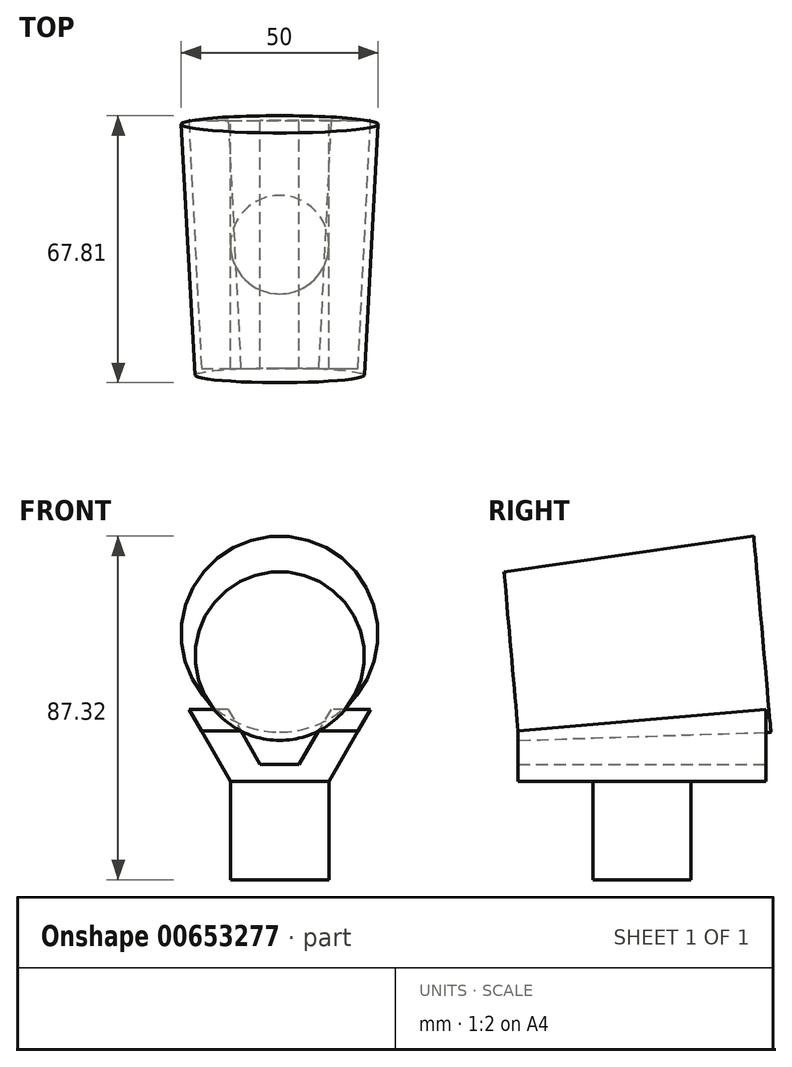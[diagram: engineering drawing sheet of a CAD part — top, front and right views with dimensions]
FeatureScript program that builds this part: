
annotation { "Feature Type Name" : "Feature", "Feature Type Description" : "" }
export const myFeature = defineFeature(function(context is Context, id is Id, definition is map)
    precondition{}
    {
        {
            var Q0;
            Q0=qCreatedBy(makeId("Top.planeOp"),FACE);
            var sketch = newSketch(context, id + "F0", { "sketchPlane" : qUnion([Q0])});
            skCircle(sketch, "E0", {"center": v(0, 0) * mm, "radius": 12.5 * mm});
            skPoint(sketch, "E1", {"position": v(12.5, 0) * mm});
            skPoint(sketch, "E2", {"position": v(-12.5, 0) * mm});
            skSolve(sketch);
        }
        {
            var Q0;
            Q0=qCreatedBy(makeId("Front.planeOp"),FACE);
            var sketch = newSketch(context, id + "F1", { "sketchPlane" : qUnion([Q0])});
            skLineSegment(sketch, "E3", {"start": v(12.5, 0) * mm, "end": v(23.08, 18.32) * mm});
            skLineSegment(sketch, "E4", {"start": v(23.08, 18.32) * mm, "end": v(13.05, 18.32) * mm});
            skLineSegment(sketch, "E5", {"start": v(-23.08, 18.32) * mm, "end": v(-12.5, 0) * mm});
            skLineSegment(sketch, "E6", {"start": v(0, -26.28) * mm, "end": v(0, 54.16) * mm, "construction": true});
            skLineSegment(sketch, "E7", {"start": v(13.05, 18.32) * mm, "end": v(4.94, 4.27) * mm});
            skLineSegment(sketch, "E8.MirrorCS", {"start": v(-13.05, 18.32) * mm, "end": v(-4.94, 4.27) * mm});
            skLineSegment(sketch, "E9.trimOffspring", {"start": v(-13.05, 18.32) * mm, "end": v(-23.08, 18.32) * mm});
            skLineSegment(sketch, "E10", {"start": v(4.94, 4.27) * mm, "end": v(-4.94, 4.27) * mm});
            skPoint(sketch, "E11.orphan", {"position": v(2.47, 0) * mm});
            skPoint(sketch, "E12.orphan", {"position": v(-2.47, 0) * mm});
            skLineSegment(sketch, "E13", {"start": v(-12.5, 0) * mm, "end": v(12.5, 0) * mm});
            skSolve(sketch);
        }
        {
            var Q0;
            Q0=makeQuery(id+"F0.imprint","IMPRINT",FACE,{"disambiguationData":[TD([[makeQuery(id+"F0.imprint","IMPRINT",EDGE,{"derivedFrom":sQuery(id+"F0.wireOp",EDGE,"E0")}),1.0]])]});
            extrude(context, id + "F2", {"entities" : qUnion([Q0]), "oppositeDirection" : true, "depth" : 25 * mm, "offsetDistance" : 25 * mm});
        }
        {
            var Q0;
            Q0=makeQuery(id+"F1.imprint","IMPRINT",FACE,{"disambiguationData":[TD([[makeQuery(id+"F1.imprint","IMPRINT",EDGE,{"derivedFrom":sQuery(id+"F1.wireOp",EDGE,"E3")}),1.0]])]});
            extrude(context, id + "F3", {"entities" : qUnion([Q0]), "operationType" : NewBodyOperationType.ADD, "endBound" : BoundingType.SYMMETRIC, "depth" : 63 * mm, "offsetDistance" : 25 * mm});
        }
        {
            var Q0;
            Q0=qCreatedBy(makeId("Right.planeOp"),FACE);
            var sketch = newSketch(context, id + "F4", { "sketchPlane" : qUnion([Q0])});
            skPoint(sketch, "E14.0", {"position": v(31.5, 18.32) * mm});
            skLineSegment(sketch, "E15.0", {"start": v(-31.5, 18.32) * mm, "end": v(-31.5, 4.27) * mm});
            skLineSegment(sketch, "E16", {"start": v(31.5, 18.32) * mm, "end": v(-31.5, 12.8) * mm});
            skLineSegment(sketch, "E17", {"start": v(-31.5, 12.8) * mm, "end": v(-31.5, 41.05) * mm});
            skLineSegment(sketch, "E18", {"start": v(31.5, 18.32) * mm, "end": v(31.5, 41.05) * mm});
            skLineSegment(sketch, "E19", {"start": v(31.5, 41.05) * mm, "end": v(-31.5, 41.05) * mm});
            skSolve(sketch);
        }
        {
            var Q0;
            {var subQ0=sQuery(id+"F4.wireOp",EDGE,"E16");Q0=makeQuery(id+"F4.imprint","IMPRINT",FACE,{"disambiguationData":[TD([[makeQuery(id+"F4.imprint","IMPRINT",EDGE,{"derivedFrom":subQ0}),-1.0]])]});}
            extrude(context, id + "F5", {"entities" : qUnion([Q0]), "operationType" : NewBodyOperationType.REMOVE, "endBound" : BoundingType.SYMMETRIC, "oppositeDirection" : true, "depth" : 100 * mm, "offsetDistance" : 25 * mm});
        }
        {
            var Q0;
            Q0=sQuery(id+"F4.wireOp",EDGE,"E16");
            var Q1;
            Q1=sQuery(id+"F4.wireOp",VERTEX,"E17.start");
            cPlane(context, id + "F6", {"entities" : qUnion([Q0, Q1]), "cplaneType" : CPlaneType.LINE_POINT, "offset" : 25 * mm, "width" : 150 * mm, "height" : 150 * mm});
        }
        {
            var Q0;
            Q0=qCreatedBy(id+"F6.planeOp",FACE);
            var sketch = newSketch(context, id + "F7", { "sketchPlane" : qUnion([Q0])});
            skLineSegment(sketch, "E20", {"start": v(0, 50.8) * mm, "end": v(0, -41.87) * mm, "construction": true});
            skPoint(sketch, "E21.1", {"position": v(9.87, 15.5) * mm});
            skCircle(sketch, "E22", {"center": v(0, 34.6) * mm, "radius": 21.5 * mm});
            skSolve(sketch);
        }
        {
            var Q0;
            Q0=qCreatedBy(id+"F6.planeOp",FACE);
            cPlane(context, id + "F8", {"entities" : qUnion([Q0]), "cplaneType" : CPlaneType.OFFSET, "offset" : 64 * mm, "oppositeDirection" : true, "width" : 150 * mm, "height" : 150 * mm});
        }
        {
            var Q0;
            Q0=qCreatedBy(id+"F8.planeOp",FACE);
            var sketch = newSketch(context, id + "F9", { "sketchPlane" : qUnion([Q0])});
            skPoint(sketch, "E23.0", {"position": v(0, 34.6) * mm});
            skCircle(sketch, "E24", {"center": v(0, 34.6) * mm, "radius": 25 * mm});
            skSolve(sketch);
        }
        {
            var Q1;
            Q1=makeQuery(id+"F9.imprint","IMPRINT",FACE,{"disambiguationData":[TD([[makeQuery(id+"F9.imprint","IMPRINT",EDGE,{"derivedFrom":sQuery(id+"F9.wireOp",EDGE,"E24")}),1.0]])]});
            var Q2;
            Q2=makeQuery(id+"F7.imprint","IMPRINT",FACE,{"disambiguationData":[TD([[makeQuery(id+"F7.imprint","IMPRINT",EDGE,{"derivedFrom":sQuery(id+"F7.wireOp",EDGE,"E22")}),1.0]])]});
            loft(context, id + "F10", {"sheetProfilesArray" : [{ "sheetProfileEntities" : qUnion([Q1]) }, { "sheetProfileEntities" : qUnion([Q2]) }]});
        }
    });
